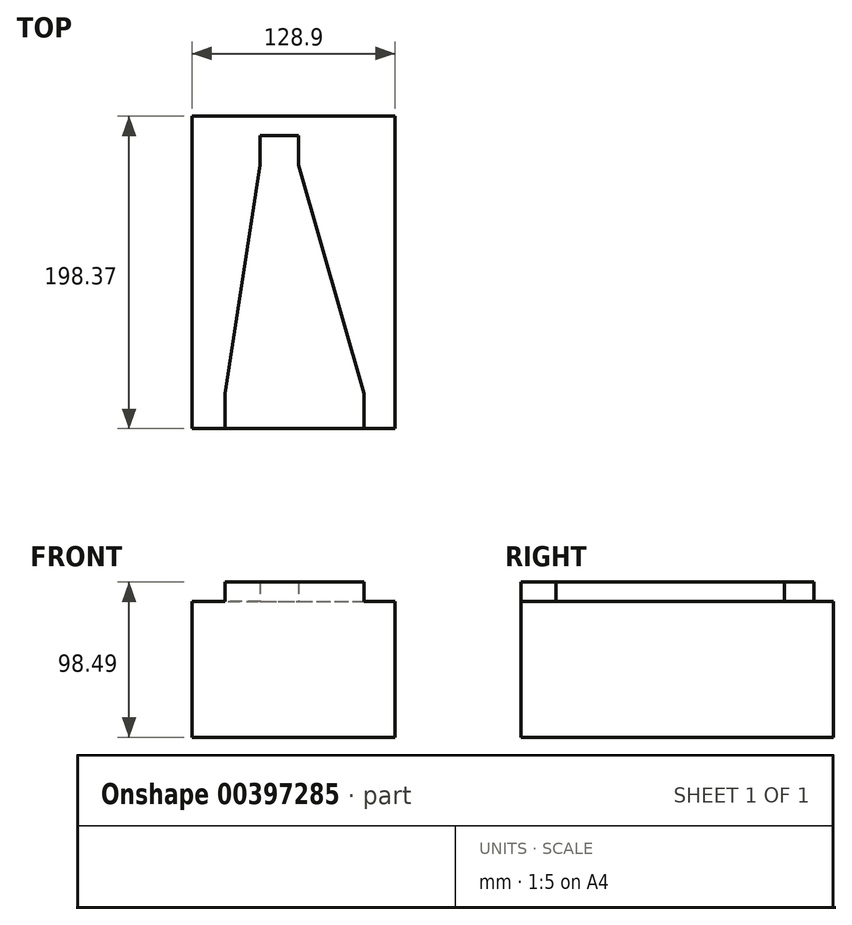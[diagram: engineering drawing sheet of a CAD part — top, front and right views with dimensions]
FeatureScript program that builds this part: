
annotation { "Feature Type Name" : "Feature", "Feature Type Description" : "" }
export const myFeature = defineFeature(function(context is Context, id is Id, definition is map)
    precondition{}
    {
        {
            var Q0;
            Q0=qCreatedBy(makeId("Front.planeOp"),FACE);
            var sketch = newSketch(context, id + "F0", { "sketchPlane" : qUnion([Q0])});
            skLineSegment(sketch, "E0.bottom", {"start": v(0, 0) * mm, "end": v(128.9, 0) * mm});
            skLineSegment(sketch, "E0.top", {"start": v(0, 86.3) * mm, "end": v(128.9, 86.3) * mm});
            skLineSegment(sketch, "E0.left", {"start": v(0, 0) * mm, "end": v(0, 86.3) * mm});
            skLineSegment(sketch, "E0.right", {"start": v(128.9, 0) * mm, "end": v(128.9, 86.3) * mm});
            skSolve(sketch);
        }
        {
            var Q0;
            Q0 = qSketchRegion(id + "F0", true);
            extrude(context, id + "F1", {"entities" : qUnion([Q0]), "depth" : 198.37 * mm});
        }
        {
            var Q0;
            Q0=makeQuery(id+"F1.opExtrude","SWEPT_FACE",FACE,{"disambiguationData":[OSD([sQuery(id+"F0.wireOp",EDGE,"E0.top")])]});
            var sketch = newSketch(context, id + "F2", { "sketchPlane" : qUnion([Q0])});
            skLineSegment(sketch, "E1.bottom", {"start": v(20.9, -176.08) * mm, "end": v(109.16, -176.08) * mm});
            skLineSegment(sketch, "E1.top", {"start": v(20.9, -198.37) * mm, "end": v(109.16, -198.37) * mm});
            skLineSegment(sketch, "E1.left", {"start": v(20.9, -176.08) * mm, "end": v(20.9, -198.37) * mm});
            skLineSegment(sketch, "E1.right", {"start": v(109.16, -176.08) * mm, "end": v(109.16, -198.37) * mm});
            skLineSegment(sketch, "E2.bottom", {"start": v(43.15, -12.35) * mm, "end": v(67.5, -12.35) * mm});
            skLineSegment(sketch, "E2.top", {"start": v(43.15, -30.9) * mm, "end": v(67.5, -30.9) * mm});
            skLineSegment(sketch, "E2.left", {"start": v(43.15, -12.35) * mm, "end": v(43.15, -30.9) * mm});
            skLineSegment(sketch, "E2.right", {"start": v(67.5, -12.35) * mm, "end": v(67.5, -30.9) * mm});
            skSolve(sketch);
        }
        {
            var Q0;
            Q0=makeQuery(id+"F2.imprint","IMPRINT",FACE,{"disambiguationData":[TD([[makeQuery(id+"F2.imprint","IMPRINT",EDGE,{"derivedFrom":sQuery(id+"F2.wireOp",EDGE,"E1.bottom")}),-1.0]])]});
            var Q1;
            Q1=makeQuery(id+"F2.imprint","IMPRINT",FACE,{"disambiguationData":[TD([[makeQuery(id+"F2.imprint","IMPRINT",EDGE,{"derivedFrom":sQuery(id+"F2.wireOp",EDGE,"E2.bottom")}),-1.0]])]});
            extrude(context, id + "F3", {"entities" : qUnion([Q0, Q1]), "operationType" : NewBodyOperationType.ADD, "depth" : 12.2 * mm});
        }
        {
            var Q1;
            Q1=makeQuery(id+"F3.opExtrude","SWEPT_FACE",FACE,{"disambiguationData":[OSD([sQuery(id+"F2.wireOp",EDGE,"E2.top")])]});
            var Q2;
            Q2=makeQuery(id+"F3.opExtrude","SWEPT_FACE",FACE,{"disambiguationData":[OSD([sQuery(id+"F2.wireOp",EDGE,"E1.bottom")])]});
            loft(context, id + "F4", {"operationType" : NewBodyOperationType.ADD, "sheetProfilesArray" : [{ "sheetProfileEntities" : qUnion([Q1]) }, { "sheetProfileEntities" : qUnion([Q2]) }]});
        }
    });
